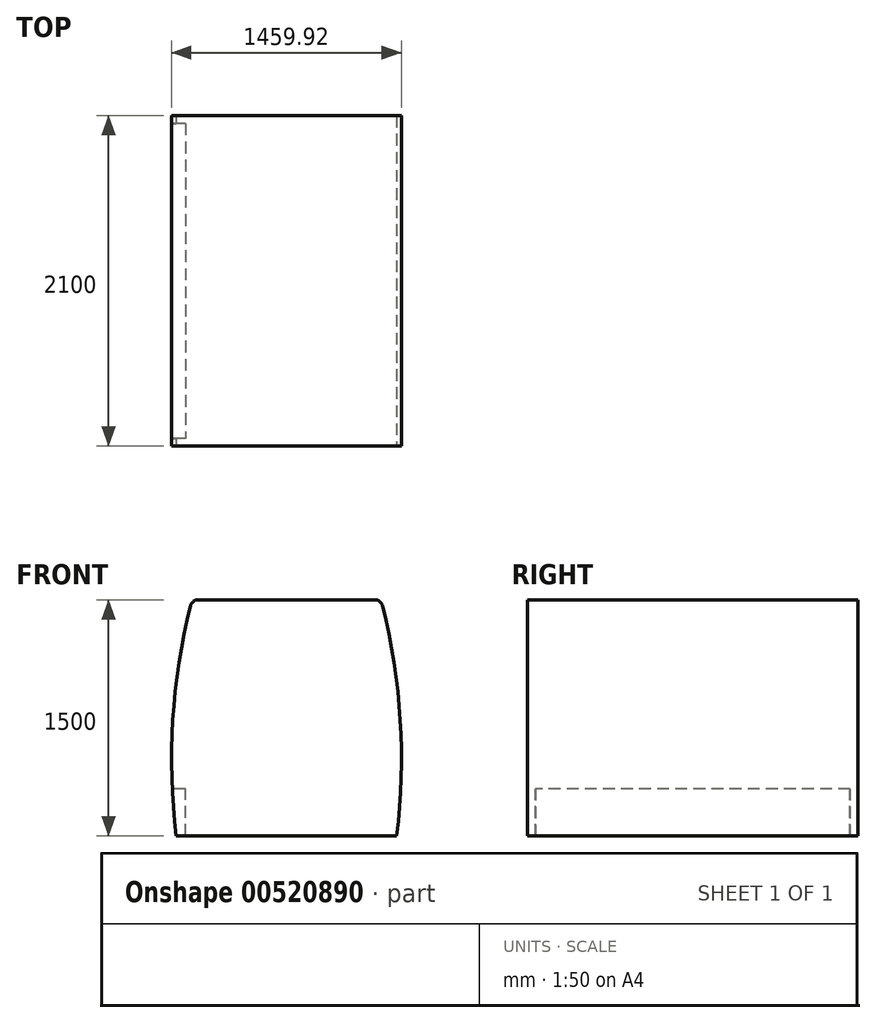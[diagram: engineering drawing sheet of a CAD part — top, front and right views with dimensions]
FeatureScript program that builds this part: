
annotation { "Feature Type Name" : "Feature", "Feature Type Description" : "" }
export const myFeature = defineFeature(function(context is Context, id is Id, definition is map)
    precondition{}
    {
        {
            var Q0;
            Q0=qCreatedBy(makeId("Front.planeOp"),FACE);
            var sketch = newSketch(context, id + "F0", { "sketchPlane" : qUnion([Q0])});
            skLineSegment(sketch, "E0", {"start": v(-700, 0) * mm, "end": v(700, 0) * mm});
            skLineSegment(sketch, "E1", {"start": v(0, 0) * mm, "end": v(0, 1500) * mm, "construction": true});
            skLineSegment(sketch, "E2", {"start": v(-600, 1500) * mm, "end": v(600, 1500) * mm});
            skArc(sketch, "E3", {"start": v(-600, 1500) * mm, "mid": v(-721.1, 754.74) * mm, "end": v(-700, 0) * mm});
            skArc(sketch, "E4", {"start": v(700, 0) * mm, "mid": v(721.1, 754.74) * mm, "end": v(600, 1500) * mm});
            skSolve(sketch);
        }
        {
            var Q0;
            Q0=makeQuery(id+"F0.imprint","IMPRINT",FACE,{"disambiguationData":[TD([[makeQuery(id+"F0.imprint","IMPRINT",EDGE,{"derivedFrom":sQuery(id+"F0.wireOp",EDGE,"E0")}),1.0]])]});
            extrude(context, id + "F1", {"entities" : qUnion([Q0]), "endBound" : BoundingType.SYMMETRIC, "oppositeDirection" : true, "depth" : 2100 * mm, "offsetDistance" : 25 * mm});
        }
        {
            var Q0;
            Q0=qCreatedBy(makeId("Front.planeOp"),FACE);
            var sketch = newSketch(context, id + "F2", { "sketchPlane" : qUnion([Q0])});
            skLineSegment(sketch, "E5.bottom", {"start": v(-642.05, 0) * mm, "end": v(-842.05, 0) * mm});
            skLineSegment(sketch, "E5.top", {"start": v(-642.05, 300) * mm, "end": v(-842.05, 300) * mm});
            skLineSegment(sketch, "E5.left", {"start": v(-642.05, 0) * mm, "end": v(-642.05, 300) * mm});
            skLineSegment(sketch, "E5.right", {"start": v(-842.05, 0) * mm, "end": v(-842.05, 300) * mm});
            skSolve(sketch);
        }
        {
            var Q0;
            Q0 = qSketchRegion(id + "F2", true);
            extrude(context, id + "F3", {"entities" : qUnion([Q0]), "operationType" : NewBodyOperationType.REMOVE, "endBound" : BoundingType.SYMMETRIC, "oppositeDirection" : true, "depth" : 2000 * mm, "offsetDistance" : 25 * mm});
        }
        {
            var Q0;
            Q0=makeQuery(id+"F1.opExtrude","SWEPT_EDGE",EDGE,{"disambiguationData":[OSD([sQuery(id+"F0.wireOp",EDGE,"E2"),sQuery(id+"F0.wireOp",EDGE,"E4")])]});
            var Q1;
            Q1=makeQuery(id+"F1.opExtrude","SWEPT_EDGE",EDGE,{"disambiguationData":[OSD([sQuery(id+"F0.wireOp",EDGE,"E2"),sQuery(id+"F0.wireOp",EDGE,"E3")])]});
            fillet(context, id + "F4", {"entities" : qUnion([Q0, Q1]), "radius" : 50 * mm, "tangentPropagation" : true, "allowEdgeOverflow" : false});
        }
    });
